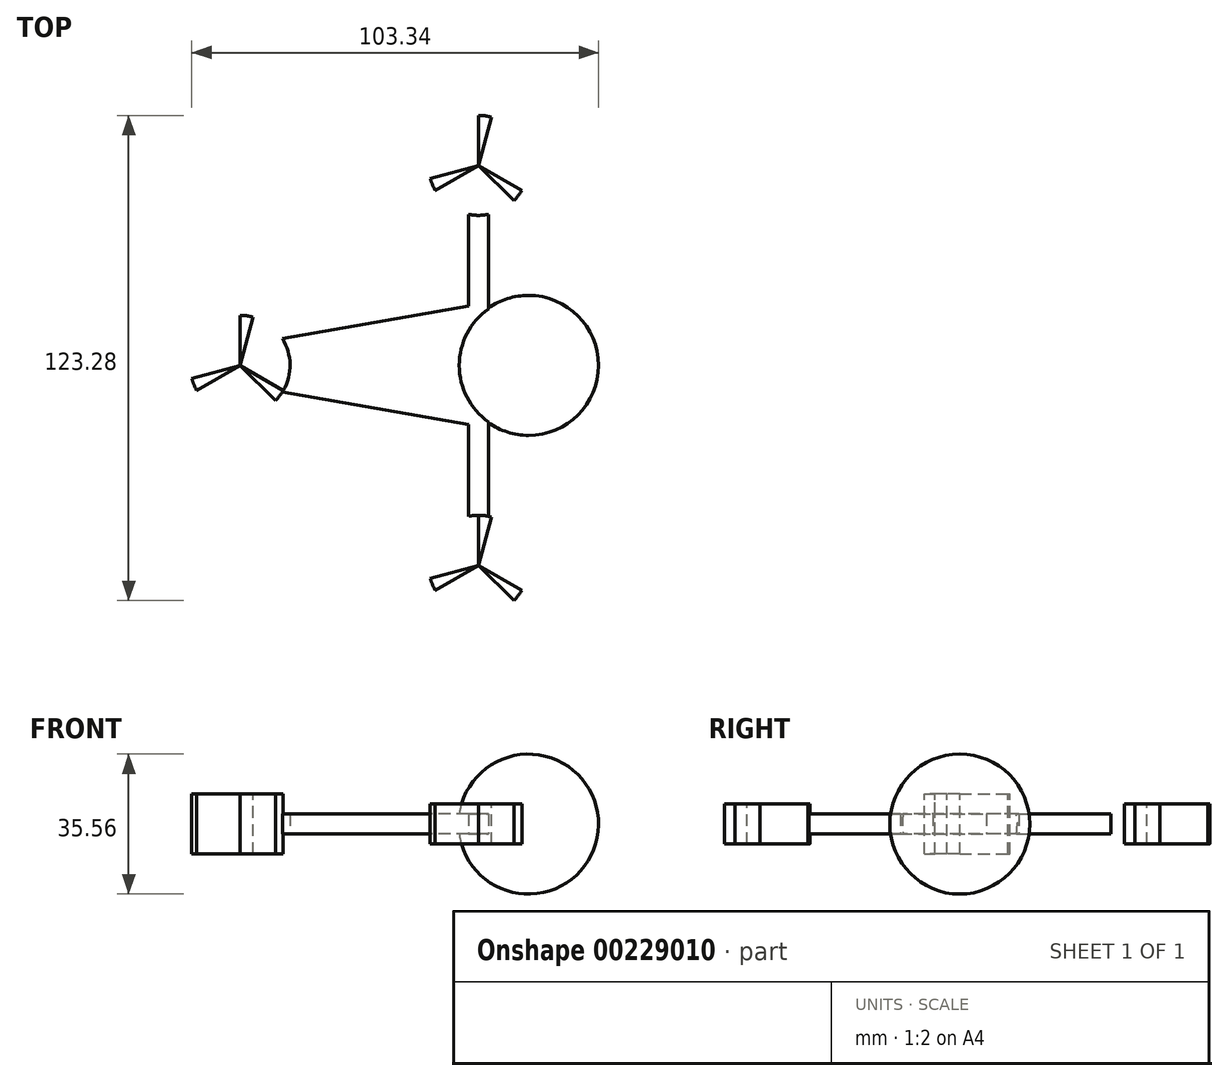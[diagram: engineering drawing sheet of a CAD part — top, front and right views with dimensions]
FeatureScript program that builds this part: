
annotation { "Feature Type Name" : "Feature", "Feature Type Description" : "" }
export const myFeature = defineFeature(function(context is Context, id is Id, definition is map)
    precondition{}
    {
        {
            var Q0;
            Q0=qCreatedBy(makeId("Top.planeOp"),FACE);
            var sketch = newSketch(context, id + "F0", { "sketchPlane" : qUnion([Q0])});
            skArc(sketch, "E0", {"start": v(0, -17.78) * mm, "mid": v(17.78, 0) * mm, "end": v(0, 17.78) * mm});
            skLineSegment(sketch, "E1", {"start": v(0, 0) * mm, "end": v(0, 17.78) * mm});
            skLineSegment(sketch, "E2", {"start": v(0, 0) * mm, "end": v(0, -17.78) * mm});
            skLineSegment(sketch, "E3", {"start": v(0, -17.78) * mm, "end": v(-62.54, -6.75) * mm});
            skLineSegment(sketch, "E4", {"start": v(0, 17.78) * mm, "end": v(-62.54, 6.75) * mm});
            skLineSegment(sketch, "E5", {"start": v(0, 0) * mm, "end": v(-73.3, 0) * mm, "construction": true});
            skCircle(sketch, "E6", {"center": v(-73.3, 0) * mm, "radius": 12.7 * mm});
            skPoint(sketch, "E7", {"position": v(-12.7, 0) * mm});
            skLineSegment(sketch, "E8", {"start": v(-12.7, 0) * mm, "end": v(-12.7, 50.8) * mm, "construction": true});
            skLineSegment(sketch, "E9", {"start": v(-12.7, 0) * mm, "end": v(-12.7, -50.8) * mm, "construction": true});
            skCircle(sketch, "E10", {"center": v(-12.7, 50.8) * mm, "radius": 12.7 * mm});
            skCircle(sketch, "E11", {"center": v(-12.7, -50.8) * mm, "radius": 12.7 * mm});
            skLineSegment(sketch, "E12", {"start": v(-12.7, -50.8) * mm, "end": v(-12.7, -38.1) * mm});
            skPoint(sketch, "E13", {"position": v(-10.16, 0) * mm});
            skPoint(sketch, "E14", {"position": v(-15.24, 0) * mm});
            skLineSegment(sketch, "E15", {"start": v(-10.16, 0) * mm, "end": v(-10.16, 47.2) * mm});
            skLineSegment(sketch, "E16", {"start": v(-15.24, 0) * mm, "end": v(-15.24, 46.64) * mm});
            skLineSegment(sketch, "E17", {"start": v(-15.24, 46.64) * mm, "end": v(-10.16, 47.2) * mm});
            skLineSegment(sketch, "E18", {"start": v(-10.16, 0) * mm, "end": v(-10.16, -45.21) * mm});
            skLineSegment(sketch, "E19", {"start": v(-15.24, 0) * mm, "end": v(-15.24, -44.45) * mm});
            skPoint(sketch, "E19.endSnap0", {"position": v(-12.7, -44.45) * mm});
            skLineSegment(sketch, "E20", {"start": v(-15.24, -44.45) * mm, "end": v(-10.16, -45.21) * mm});
            skSolve(sketch);
        }
        {
            var Q0;
            Q0=makeQuery(id+"F0.imprint","IMPRINT",FACE,{"disambiguationData":[TD([[makeQuery(id+"F0.imprint","IMPRINT",EDGE,{"derivedFrom":sQuery(id+"F0.wireOp",EDGE,"E0")}),1.0]])]});
            var Q1;
            Q1=sQuery(id+"F0.wireOp",EDGE,"E2");
            revolve(context, id + "F1", {"entities" : qUnion([Q0]), "axis" : qUnion([Q1]), "revolveType" : RevolveType.FULL});
        }
        {
            var Q0;
            {var subQ0=sQuery(id+"F0.wireOp",EDGE,"E15");var subQ1=sQuery(id+"F0.wireOp",EDGE,"E4");var subQ2=makeQuery(id+"F0.imprint","INTERSECT",VERTEX,{"derivedFrom":[subQ1,subQ0]});Q0=makeQuery(id+"F0.imprint","IMPRINT",FACE,{"disambiguationData":[TD([[makeQuery(id+"F0.imprint","IMPRINT",EDGE,{"disambiguationData":[TD([[subQ2,-1.0]])],"derivedFrom":subQ1}),-1.0]])]});}
            var Q1;
            {var subQ0=sQuery(id+"F0.wireOp",EDGE,"E18");var subQ5=sQuery(id+"F0.wireOp",EDGE,"E3");var subQ6=makeQuery(id+"F0.imprint","INTERSECT",VERTEX,{"derivedFrom":[subQ5,subQ0]});Q1=makeQuery(id+"F0.imprint","IMPRINT",FACE,{"disambiguationData":[TD([[makeQuery(id+"F0.imprint","IMPRINT",EDGE,{"disambiguationData":[TD([[subQ6,-1.0]])],"derivedFrom":subQ5}),-1.0]])]});}
            var Q2;
            {var subQ0=sQuery(id+"F0.wireOp",EDGE,"E6");var subQ1=sQuery(id+"F0.wireOp",EDGE,"E3");var subQ2=makeQuery(id+"F0.imprint","INTERSECT",VERTEX,{"derivedFrom":[subQ1,subQ0]});Q2=makeQuery(id+"F0.imprint","IMPRINT",FACE,{"disambiguationData":[TD([[makeQuery(id+"F0.imprint","IMPRINT",EDGE,{"disambiguationData":[TD([[subQ2,1.0]])],"derivedFrom":subQ1}),-1.0]])]});}
            var Q3;
            {var subQ0=sQuery(id+"F0.wireOp",EDGE,"E18");var subQ1=sQuery(id+"F0.wireOp",EDGE,"E3");var subQ2=makeQuery(id+"F0.imprint","INTERSECT",VERTEX,{"derivedFrom":[subQ1,subQ0]});Q3=makeQuery(id+"F0.imprint","IMPRINT",FACE,{"disambiguationData":[TD([[makeQuery(id+"F0.imprint","IMPRINT",EDGE,{"disambiguationData":[TD([[subQ2,-1.0]])],"derivedFrom":subQ1}),1.0]])]});}
            extrude(context, id + "F2", {"entities" : qUnion([Q0, Q1, Q2, Q3]), "operationType" : NewBodyOperationType.ADD, "endBound" : BoundingType.SYMMETRIC, "depth" : 5.08 * mm});
        }
        {
            var Q0;
            {var subQ5=sQuery(id+"F0.wireOp",EDGE,"E17");Q0=makeQuery(id+"F0.imprint","IMPRINT",FACE,{"disambiguationData":[TD([[makeQuery(id+"F0.imprint","IMPRINT",EDGE,{"derivedFrom":subQ5}),1.0]])]});}
            var Q1;
            {var subQ1=sQuery(id+"F0.wireOp",EDGE,"E18");var subQ3=sQuery(id+"F0.wireOp",EDGE,"E11");var subQ4=makeQuery(id+"F0.imprint","INTERSECT",VERTEX,{"derivedFrom":[subQ3,subQ1]});Q1=makeQuery(id+"F0.imprint","IMPRINT",FACE,{"disambiguationData":[TD([[makeQuery(id+"F0.imprint","IMPRINT",EDGE,{"disambiguationData":[TD([[subQ4,1.0]])],"derivedFrom":subQ3}),1.0]])]});}
            var Q2;
            {var subQ5=sQuery(id+"F0.wireOp",EDGE,"E17");Q2=makeQuery(id+"F0.imprint","IMPRINT",FACE,{"disambiguationData":[TD([[makeQuery(id+"F0.imprint","IMPRINT",EDGE,{"derivedFrom":subQ5}),-1.0]])]});}
            var Q3;
            {var subQ0=sQuery(id+"F0.wireOp",EDGE,"E12");var subQ1=sQuery(id+"F0.wireOp",EDGE,"E11");var subQ2=makeQuery(id+"F0.imprint","INTERSECT",VERTEX,{"derivedFrom":[subQ1,subQ0]});Q3=makeQuery(id+"F0.imprint","IMPRINT",FACE,{"disambiguationData":[TD([[makeQuery(id+"F0.imprint","IMPRINT",EDGE,{"disambiguationData":[TD([[subQ2,-1.0]])],"derivedFrom":subQ1}),1.0]])]});}
            var Q4;
            {var subQ0=sQuery(id+"F0.wireOp",EDGE,"E12");var subQ1=sQuery(id+"F0.wireOp",EDGE,"E11");var subQ2=makeQuery(id+"F0.imprint","INTERSECT",VERTEX,{"derivedFrom":[subQ1,subQ0]});Q4=makeQuery(id+"F0.imprint","IMPRINT",FACE,{"disambiguationData":[TD([[makeQuery(id+"F0.imprint","IMPRINT",EDGE,{"disambiguationData":[TD([[subQ2,1.0]])],"derivedFrom":subQ1}),1.0]])]});}
            extrude(context, id + "F3", {"entities" : qUnion([Q0, Q1, Q2, Q3, Q4]), "endBound" : BoundingType.SYMMETRIC, "depth" : 10.16 * mm});
        }
        {
            var Q0;
            {var subQ0=sQuery(id+"F0.wireOp",EDGE,"E6");var subQ1=makeQuery(id+"F0.imprint","INTERSECT",VERTEX,{"derivedFrom":[sQuery(id+"F0.wireOp",EDGE,"E3"),subQ0]});Q0=makeQuery(id+"F0.imprint","IMPRINT",FACE,{"disambiguationData":[TD([[makeQuery(id+"F0.imprint","IMPRINT",EDGE,{"disambiguationData":[TD([[subQ1,1.0]])],"derivedFrom":subQ0}),1.0]])]});}
            extrude(context, id + "F4", {"entities" : qUnion([Q0]), "endBound" : BoundingType.SYMMETRIC, "depth" : 15.24 * mm});
        }
        {
            var Q0;
            Q0=makeQuery(id+"F4.opExtrude","CAP_FACE",FACE,{"disambiguationData":[OSD([sQuery(id+"F0.wireOp",EDGE,"E6")])],"isStart":false});
            var sketch = newSketch(context, id + "F5", { "sketchPlane" : qUnion([Q0])});
            skLineSegment(sketch, "E21", {"start": v(-73.3, 0) * mm, "end": v(-73.3, 12.7) * mm});
            skLineSegment(sketch, "E22", {"start": v(-73.3, 0) * mm, "end": v(-62.3, -6.35) * mm});
            skLineSegment(sketch, "E23", {"start": v(-73.3, 0) * mm, "end": v(-84.29, -6.35) * mm});
            skLineSegment(sketch, "E24", {"start": v(-73.3, 0) * mm, "end": v(-70, 12.27) * mm});
            skLineSegment(sketch, "E25", {"start": v(-73.3, 0) * mm, "end": v(-64.31, -8.98) * mm});
            skLineSegment(sketch, "E26", {"start": v(-73.3, 0) * mm, "end": v(-85.56, -3.29) * mm});
            skCircle(sketch, "E27", {"center": v(-73.3, 0) * mm, "radius": 12.7 * mm});
            skSolve(sketch);
        }
        {
            var Q0;
            Q0=makeQuery(id+"F3.opExtrude","CAP_FACE",FACE,{"disambiguationData":[OSD([sQuery(id+"F0.wireOp",EDGE,"E11")])],"isStart":false});
            var sketch = newSketch(context, id + "F6", { "sketchPlane" : qUnion([Q0])});
            skLineSegment(sketch, "E28", {"start": v(-12.7, -50.8) * mm, "end": v(-12.7, -38.1) * mm});
            skLineSegment(sketch, "E29", {"start": v(-12.7, -50.8) * mm, "end": v(-1.7, -57.15) * mm});
            skLineSegment(sketch, "E30", {"start": v(-12.7, -50.8) * mm, "end": v(-23.7, -57.15) * mm});
            skLineSegment(sketch, "E31", {"start": v(-12.7, -50.8) * mm, "end": v(-9.41, -38.53) * mm});
            skLineSegment(sketch, "E32", {"start": v(-12.7, -50.8) * mm, "end": v(-3.72, -59.78) * mm});
            skLineSegment(sketch, "E33", {"start": v(-12.7, -50.8) * mm, "end": v(-24.97, -54.09) * mm});
            skCircle(sketch, "E34", {"center": v(-12.7, -50.8) * mm, "radius": 12.7 * mm});
            skSolve(sketch);
        }
        {
            var Q0;
            Q0=makeQuery(id+"F3.opExtrude","CAP_FACE",FACE,{"disambiguationData":[OSD([sQuery(id+"F0.wireOp",EDGE,"E10")])],"isStart":false});
            var sketch = newSketch(context, id + "F7", { "sketchPlane" : qUnion([Q0])});
            skLineSegment(sketch, "E35", {"start": v(-12.7, 50.8) * mm, "end": v(-12.7, 63.5) * mm});
            skLineSegment(sketch, "E36", {"start": v(-12.7, 50.8) * mm, "end": v(-1.7, 44.45) * mm});
            skLineSegment(sketch, "E37", {"start": v(-12.7, 50.8) * mm, "end": v(-23.7, 44.45) * mm});
            skLineSegment(sketch, "E38", {"start": v(-12.7, 50.8) * mm, "end": v(-9.41, 63.07) * mm});
            skLineSegment(sketch, "E39", {"start": v(-12.7, 50.8) * mm, "end": v(-3.72, 41.82) * mm});
            skLineSegment(sketch, "E40", {"start": v(-12.7, 50.8) * mm, "end": v(-24.97, 47.51) * mm});
            skCircle(sketch, "E41", {"center": v(-12.7, 50.8) * mm, "radius": 12.7 * mm});
            skSolve(sketch);
        }
        {
            var Q0;
            {var subQ0=sQuery(id+"F7.wireOp",EDGE,"E36");Q0=makeQuery(id+"F7.imprint","IMPRINT",FACE,{"disambiguationData":[TD([[makeQuery(id+"F7.imprint","IMPRINT",EDGE,{"derivedFrom":subQ0}),1.0]])]});}
            var Q1;
            {var subQ0=sQuery(id+"F7.wireOp",EDGE,"E35");Q1=makeQuery(id+"F7.imprint","IMPRINT",FACE,{"disambiguationData":[TD([[makeQuery(id+"F7.imprint","IMPRINT",EDGE,{"derivedFrom":subQ0}),1.0]])]});}
            var Q2;
            {var subQ0=sQuery(id+"F7.wireOp",EDGE,"E37");Q2=makeQuery(id+"F7.imprint","IMPRINT",FACE,{"disambiguationData":[TD([[makeQuery(id+"F7.imprint","IMPRINT",EDGE,{"derivedFrom":subQ0}),1.0]])]});}
            extrude(context, id + "F8", {"entities" : qUnion([Q0, Q1, Q2]), "operationType" : NewBodyOperationType.REMOVE, "oppositeDirection" : true, "depth" : 25.4 * mm});
        }
        {
            var Q0;
            Q0=sQuery(id+"F7.wireOp",EDGE,"E41");
            extrude(context, id + "F9", {"bodyType" : ToolBodyType.SURFACE, "surfaceEntities" : qUnion([Q0]), "oppositeDirection" : true, "depth" : 10.16 * mm});
        }
        {
            var Q0;
            {var subQ0=sQuery(id+"F6.wireOp",EDGE,"E29");Q0=makeQuery(id+"F6.imprint","IMPRINT",FACE,{"disambiguationData":[TD([[makeQuery(id+"F6.imprint","IMPRINT",EDGE,{"derivedFrom":subQ0}),1.0]])]});}
            var Q1;
            {var subQ0=sQuery(id+"F6.wireOp",EDGE,"E28");Q1=makeQuery(id+"F6.imprint","IMPRINT",FACE,{"disambiguationData":[TD([[makeQuery(id+"F6.imprint","IMPRINT",EDGE,{"derivedFrom":subQ0}),1.0]])]});}
            var Q2;
            {var subQ0=sQuery(id+"F6.wireOp",EDGE,"E30");Q2=makeQuery(id+"F6.imprint","IMPRINT",FACE,{"disambiguationData":[TD([[makeQuery(id+"F6.imprint","IMPRINT",EDGE,{"derivedFrom":subQ0}),1.0]])]});}
            extrude(context, id + "F10", {"entities" : qUnion([Q0, Q1, Q2]), "operationType" : NewBodyOperationType.REMOVE, "endBound" : BoundingType.THROUGH_ALL, "oppositeDirection" : true, "depth" : 25.4 * mm});
        }
        {
            var Q0;
            Q0=sQuery(id+"F6.wireOp",EDGE,"E34");
            extrude(context, id + "F11", {"bodyType" : ToolBodyType.SURFACE, "surfaceEntities" : qUnion([Q0]), "oppositeDirection" : true, "depth" : 10.16 * mm});
        }
        {
            var Q0;
            {var subQ0=sQuery(id+"F5.wireOp",EDGE,"E21");Q0=makeQuery(id+"F5.imprint","IMPRINT",FACE,{"disambiguationData":[TD([[makeQuery(id+"F5.imprint","IMPRINT",EDGE,{"derivedFrom":subQ0}),1.0]])]});}
            var Q1;
            {var subQ0=sQuery(id+"F5.wireOp",EDGE,"E22");Q1=makeQuery(id+"F5.imprint","IMPRINT",FACE,{"disambiguationData":[TD([[makeQuery(id+"F5.imprint","IMPRINT",EDGE,{"derivedFrom":subQ0}),1.0]])]});}
            var Q2;
            {var subQ0=sQuery(id+"F5.wireOp",EDGE,"E23");Q2=makeQuery(id+"F5.imprint","IMPRINT",FACE,{"disambiguationData":[TD([[makeQuery(id+"F5.imprint","IMPRINT",EDGE,{"derivedFrom":subQ0}),1.0]])]});}
            extrude(context, id + "F12", {"entities" : qUnion([Q0, Q1, Q2]), "operationType" : NewBodyOperationType.REMOVE, "endBound" : BoundingType.THROUGH_ALL, "oppositeDirection" : true, "depth" : 25.4 * mm});
        }
        {
            var Q0;
            {var subQ0=sQuery(id+"F5.wireOp",EDGE,"E23");Q0=makeQuery(id+"F5.imprint","IMPRINT",FACE,{"disambiguationData":[TD([[makeQuery(id+"F5.imprint","IMPRINT",EDGE,{"derivedFrom":subQ0}),-1.0]])]});}
            var sketch = newSketch(context, id + "F13", { "sketchPlane" : qUnion([Q0])});
            skCircle(sketch, "E42", {"center": v(-73.3, 0) * mm, "radius": 12.7 * mm});
            skSolve(sketch);
        }
        {
            var Q0;
            Q0 = qSketchRegion(id + "F13", true);
            var Q1;
            Q1=sQuery(id+"F13.wireOp",EDGE,"E42");
            extrude(context, id + "F14", {"entities" : qUnion([Q0]), "bodyType" : ToolBodyType.SURFACE, "surfaceEntities" : qUnion([Q1]), "oppositeDirection" : true, "depth" : 15.24 * mm});
        }
    });
